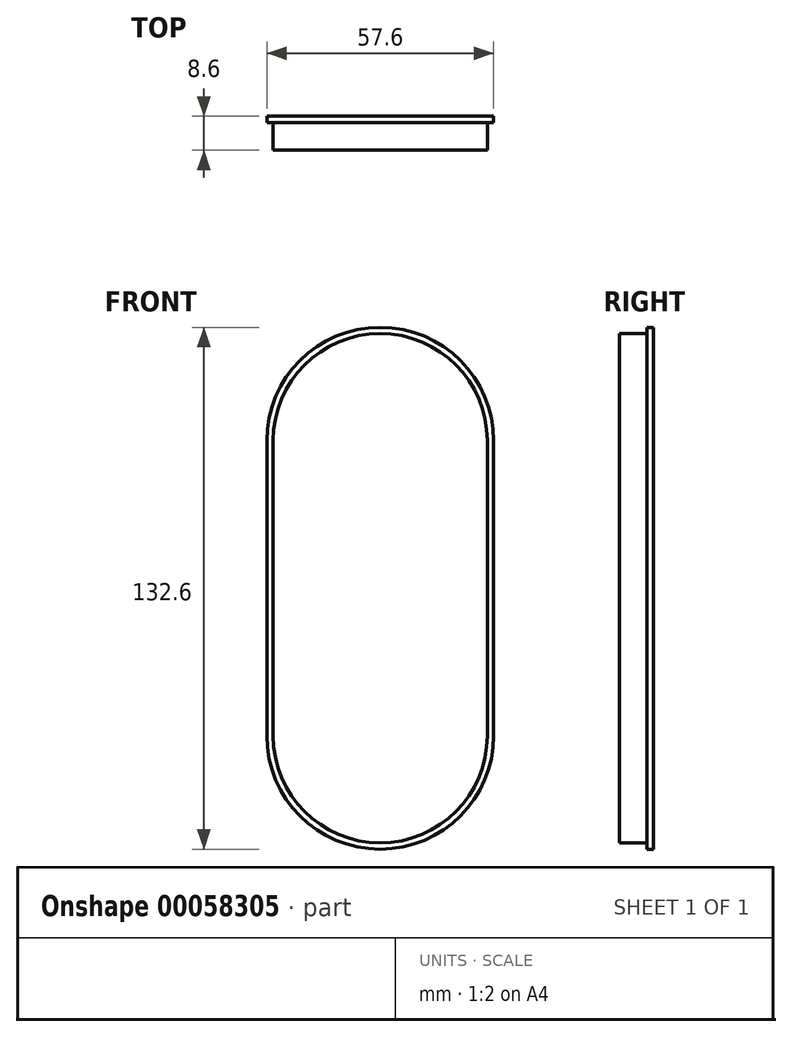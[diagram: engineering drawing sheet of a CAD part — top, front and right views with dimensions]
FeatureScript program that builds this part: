
annotation { "Feature Type Name" : "Feature", "Feature Type Description" : "" }
export const myFeature = defineFeature(function(context is Context, id is Id, definition is map)
    precondition{}
    {
        {
            assignVariable(context, id + "F0", {"name" : "wall", "anyValue" : 1.6});
        }
        {
            assignVariable(context, id + "F1", {"name" : "height", "anyValue" : 7});
        }
        {
            var Q0;
            Q0=qCreatedBy(makeId("Front.planeOp"),FACE);
            var sketch = newSketch(context, id + "F2", { "sketchPlane" : qUnion([Q0])});
            skLineSegment(sketch, "E0", {"start": v(0, 0) * mm, "end": v(0, 75) * mm, "construction": true});
            skArc(sketch, "E1.0.startCap", {"start": v(27.2, 0) * mm, "mid": v(0, -27.2) * mm, "end": v(-27.2, 0) * mm});
            skArc(sketch, "E1.0.endCap", {"start": v(-27.2, 75) * mm, "mid": v(0, 102.2) * mm, "end": v(27.2, 75) * mm});
            skLineSegment(sketch, "E1.0.left", {"start": v(-27.2, 0) * mm, "end": v(-27.2, 75) * mm});
            skLineSegment(sketch, "E1.0.right", {"start": v(27.2, 0) * mm, "end": v(27.2, 75) * mm});
            skArc(sketch, "E2.0", {"start": v(-28.8, 75) * mm, "mid": v(0, 103.8) * mm, "end": v(28.8, 75) * mm});
            skLineSegment(sketch, "E2.1", {"start": v(-28.8, 0) * mm, "end": v(-28.8, 75) * mm});
            skArc(sketch, "E2.2", {"start": v(28.8, 0) * mm, "mid": v(0, -28.8) * mm, "end": v(-28.8, 0) * mm});
            skLineSegment(sketch, "E2.3", {"start": v(28.8, 0) * mm, "end": v(28.8, 75) * mm});
            skSolve(sketch);
        }
        {
            var Q0;
            Q0=makeQuery(id+"F2.imprint","IMPRINT",FACE,{"disambiguationData":[TD([[makeQuery(id+"F2.imprint","IMPRINT",EDGE,{"derivedFrom":sQuery(id+"F2.wireOp",EDGE,"E1.0.startCap")}),1.0]])]});
            extrude(context, id + "F3", {"entities" : qUnion([Q0]), "depth" : (getVariable(context, 'height')) * mm});
        }
        {
            var Q0;
            Q0=makeQuery(id+"F2.imprint","IMPRINT",FACE,{"disambiguationData":[TD([[makeQuery(id+"F2.imprint","IMPRINT",EDGE,{"derivedFrom":sQuery(id+"F2.wireOp",EDGE,"E1.0.startCap")}),-1.0]])]});
            var Q1;
            Q1=makeQuery(id+"F2.imprint","IMPRINT",FACE,{"disambiguationData":[TD([[makeQuery(id+"F2.imprint","IMPRINT",EDGE,{"derivedFrom":sQuery(id+"F2.wireOp",EDGE,"E1.0.startCap")}),1.0]])]});
            extrude(context, id + "F4", {"entities" : qUnion([Q0, Q1]), "operationType" : NewBodyOperationType.ADD, "oppositeDirection" : true, "depth" : (getVariable(context, 'wall')) * mm});
        }
    });
